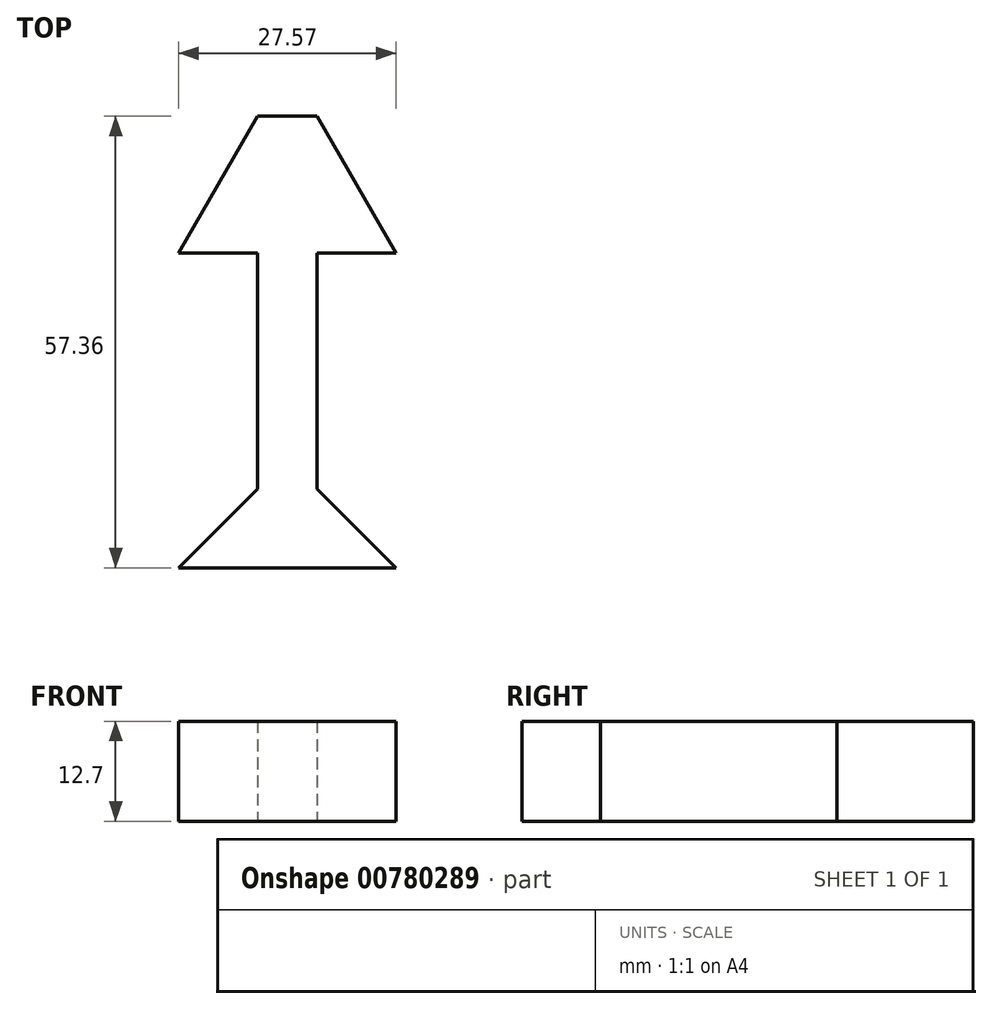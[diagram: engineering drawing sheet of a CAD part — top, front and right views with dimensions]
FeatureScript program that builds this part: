
annotation { "Feature Type Name" : "Feature", "Feature Type Description" : "" }
export const myFeature = defineFeature(function(context is Context, id is Id, definition is map)
    precondition{}
    {
        {
            var Q0;
            Q0=qCreatedBy(makeId("Top.planeOp"),FACE);
            var sketch = newSketch(context, id + "F0", { "sketchPlane" : qUnion([Q0])});
            skLineSegment(sketch, "E0", {"start": v(-10, -57.36) * mm, "end": v(0, -47.36) * mm});
            skLineSegment(sketch, "E1", {"start": v(-10, -57.36) * mm, "end": v(17.57, -57.36) * mm});
            skLineSegment(sketch, "E2", {"start": v(17.57, -57.36) * mm, "end": v(7.57, -47.36) * mm});
            skLineSegment(sketch, "E3", {"start": v(7.57, -47.36) * mm, "end": v(7.57, -17.36) * mm});
            skLineSegment(sketch, "E4", {"start": v(7.57, -17.36) * mm, "end": v(17.57, -17.36) * mm});
            skLineSegment(sketch, "E5", {"start": v(17.57, -17.36) * mm, "end": v(7.57, 0) * mm});
            skLineSegment(sketch, "E6", {"start": v(7.57, 0) * mm, "end": v(0, 0) * mm});
            skLineSegment(sketch, "E7", {"start": v(0, 0) * mm, "end": v(-10, -17.36) * mm});
            skLineSegment(sketch, "E8", {"start": v(-10, -17.36) * mm, "end": v(0, -17.36) * mm});
            skLineSegment(sketch, "E9", {"start": v(0, -17.36) * mm, "end": v(0, -47.36) * mm});
            skSolve(sketch);
        }
        {
            var Q0;
            Q0=makeQuery(id+"F0.imprint","IMPRINT",FACE,{"disambiguationData":[TD([[makeQuery(id+"F0.imprint","IMPRINT",EDGE,{"derivedFrom":sQuery(id+"F0.wireOp",EDGE,"E0")}),-1.0]])]});
            extrude(context, id + "F1", {"entities" : qUnion([Q0]), "depth" : 12.7 * mm, "offsetDistance" : 25.4 * mm});
        }
    });
